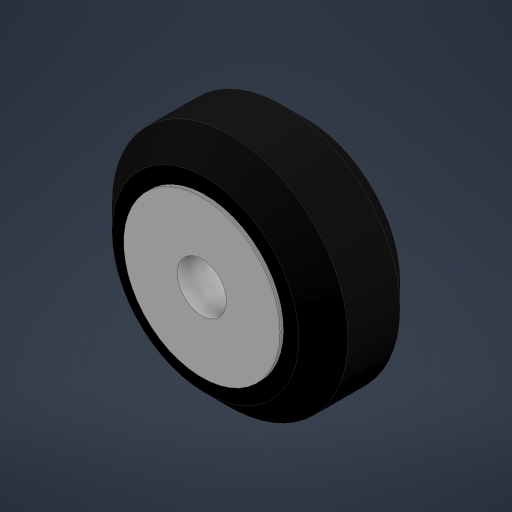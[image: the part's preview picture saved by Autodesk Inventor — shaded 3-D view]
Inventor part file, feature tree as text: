
AUTODESK INVENTOR PART (.ipt)
format: ipt  version: 2024.2 (Build 282272000, 272)  size: 207,360 bytes
history: native  units: mm
features: extrude x2, sketch x1, chamfer x1
ambient origin geometry x8: Origin, YZ Plane, XZ Plane, XY Plane, X Axis, Y Axis, Z Axis, Center Point
bodies: Solid1 (feature_tree)
feature tree (4):
  sketch  "Sketch1"  dims[d0=5.0mm d1=24.0mm d2=15.9mm d3=11.0mm d4=0.0mm d5=10.3mm d6=0.0mm d7=2.5mm d8=2.0mm d9=45.0deg]
  extrude  "Extrusion1"  Depth=2.5mm
  extrude  "Extrusion2"  Depth=2.5mm
  chamfer  "Chamfer1"  Distance=11.0mm
